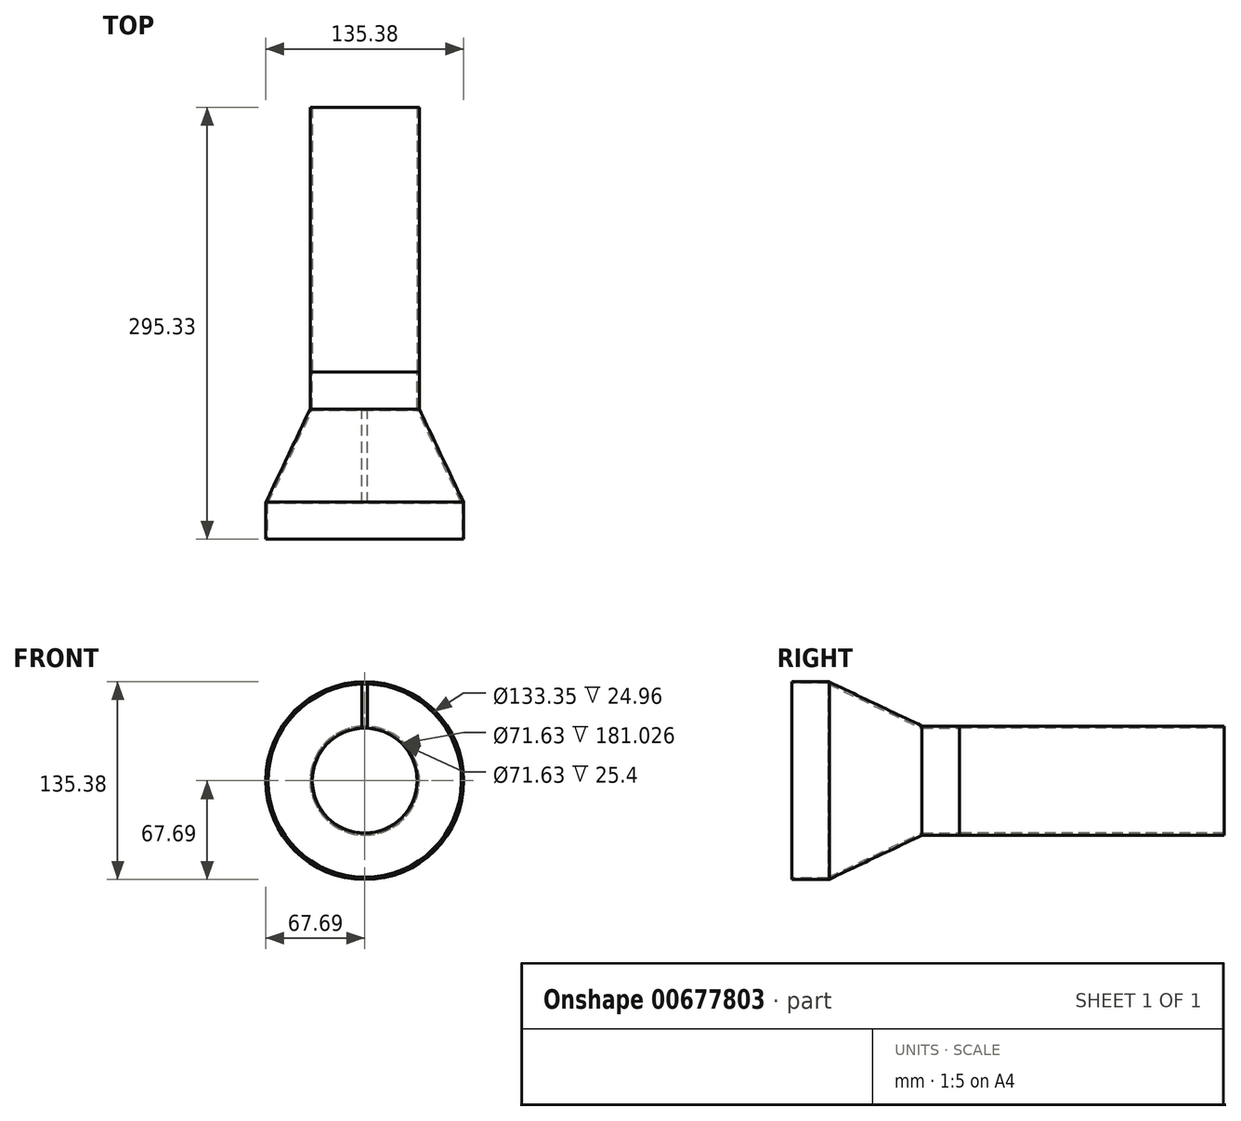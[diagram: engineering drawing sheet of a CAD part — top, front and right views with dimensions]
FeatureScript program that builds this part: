
annotation { "Feature Type Name" : "Feature", "Feature Type Description" : "" }
export const myFeature = defineFeature(function(context is Context, id is Id, definition is map)
    precondition{}
    {
        {
            var Q0;
            Q0=qCreatedBy(makeId("Front.planeOp"),FACE);
            var sketch = newSketch(context, id + "F0", { "sketchPlane" : qUnion([Q0])});
            skCircle(sketch, "E0", {"center": v(0, 0) * mm, "radius": 35.81 * mm});
            skCircle(sketch, "E1", {"center": v(0, 0) * mm, "radius": 37.26 * mm});
            skSolve(sketch);
        }
        {
            var Q0;
            Q0=qCreatedBy(makeId("Front.planeOp"),FACE);
            cPlane(context, id + "F1", {"entities" : qUnion([Q0]), "cplaneType" : CPlaneType.OFFSET, "offset" : 114.3 * mm, "width" : 152.4 * mm, "height" : 152.4 * mm});
        }
        {
            var Q0;
            Q0=qCreatedBy(id+"F1.planeOp",FACE);
            var sketch = newSketch(context, id + "F2", { "sketchPlane" : qUnion([Q0])});
            skCircle(sketch, "E2", {"center": v(0, 0) * mm, "radius": 66.68 * mm});
            skCircle(sketch, "E3", {"center": v(0, 0) * mm, "radius": 67.7 * mm});
            skSolve(sketch);
        }
        {
            var Q0;
            Q0=makeQuery(id+"F2.imprint","IMPRINT",FACE,{"disambiguationData":[TD([[makeQuery(id+"F2.imprint","IMPRINT",EDGE,{"derivedFrom":sQuery(id+"F2.wireOp",EDGE,"E2")}),-1.0]])]});
            extrude(context, id + "F3", {"entities" : qUnion([Q0]), "oppositeDirection" : true, "depth" : 25.4 * mm, "offsetDistance" : 25.4 * mm});
        }
        {
            var Q0;
            Q0=makeQuery(id+"F0.imprint","IMPRINT",FACE,{"disambiguationData":[TD([[makeQuery(id+"F0.imprint","IMPRINT",EDGE,{"derivedFrom":sQuery(id+"F0.wireOp",EDGE,"E0")}),-1.0]])]});
            extrude(context, id + "F4", {"entities" : qUnion([Q0]), "depth" : 25.4 * mm, "offsetDistance" : 25.4 * mm});
        }
        {
            var Q0;
            Q0=qCreatedBy(makeId("Right.planeOp"),FACE);
            var sketch = newSketch(context, id + "F5", { "sketchPlane" : qUnion([Q0])});
            skLineSegment(sketch, "E4", {"start": v(-113.15, 0) * mm, "end": v(0, 0) * mm});
            skLineSegment(sketch, "E5", {"start": v(-88.94, 67.48) * mm, "end": v(-25.44, 37.3) * mm});
            skSolve(sketch);
        }
        {
            var Q0;
            Q0=sQuery(id+"F5.wireOp",EDGE,"E5");
            extrude(context, id + "F6", {"bodyType" : ToolBodyType.SURFACE, "surfaceEntities" : qUnion([Q0]), "endBound" : BoundingType.SYMMETRIC, "oppositeDirection" : true, "depth" : 3.8 * mm, "offsetDistance" : 25.4 * mm});
        }
        {
            var Q0;
            Q0=makeQuery(id+"F6.opExtrude","SWEPT_FACE",FACE,{"disambiguationData":[OSD([sQuery(id+"F5.wireOp",EDGE,"E5")])]});
            extrude(context, id + "F7", {"entities" : qUnion([Q0]), "operationType" : NewBodyOperationType.ADD, "oppositeDirection" : true, "depth" : 1.59 * mm, "offsetDistance" : 25.4 * mm});
        }
        {
            var Q0;
            {var subQ0=sQuery(id+"F5.wireOp",EDGE,"E5");Q0=makeQuery(id+"F7.opExtrude","SWEPT_FACE",FACE,{"disambiguationData":[OSD([subQ0]),TDD([makeQuery(id+"F6.opExtrude","CAP_EDGE",EDGE,{"disambiguationData":[OSD([subQ0])],"isStart":true})])]});}
            var Q1;
            Q1=sQuery(id+"F5.wireOp",EDGE,"E4");
            revolve(context, id + "F8", {"operationType" : NewBodyOperationType.ADD, "entities" : qUnion([Q0]), "axis" : qUnion([Q1]), "revolveType" : RevolveType.FULL});
        }
        {
            var Q0;
            Q0=makeQuery(id+"F4.opExtrude","CAP_FACE",FACE,{"disambiguationData":[OSD([sQuery(id+"F0.wireOp",EDGE,"E0"),sQuery(id+"F0.wireOp",EDGE,"E1")])],"isStart":true});
            extrude(context, id + "F9", {"entities" : qUnion([Q0]), "depth" : 181.03 * mm, "offsetDistance" : 25.4 * mm});
        }
    });
